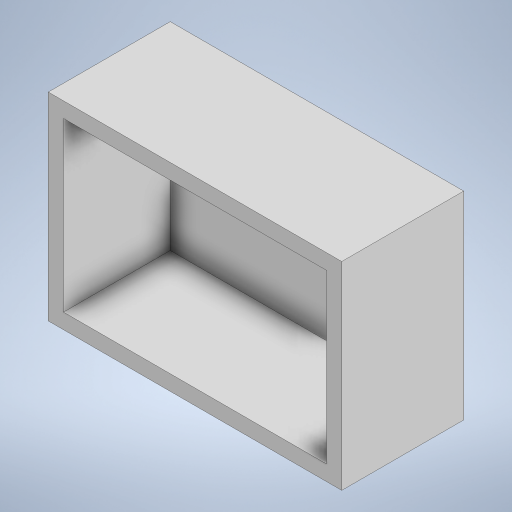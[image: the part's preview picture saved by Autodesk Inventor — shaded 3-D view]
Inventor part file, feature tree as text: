
AUTODESK INVENTOR PART (.ipt)
format: ipt  version: 2023 (Build 270158000, 158)  size: 199,168 bytes
history: native  units: mm
features: extrude x2, sketch x2
ambient origin geometry x8: Origin, YZ Plane, XZ Plane, XY Plane, X Axis, Y Axis, Z Axis, Center Point
bodies: Solid1 (feature_tree)
feature tree (4):
  extrude  "Extrusion1"  Depth=260.0mm
  extrude  "Extrusion2"  Depth=20.0mm
  sketch  "Sketch1"  dims[d0=385.0mm d1=260.0mm]
  sketch  "Sketch2"  dims[d2=160.0mm d3=0.0mm d4=20.0mm d5=20.0mm d6=20.0mm d7=20.0mm d8=140.0mm d9=0.0mm]
